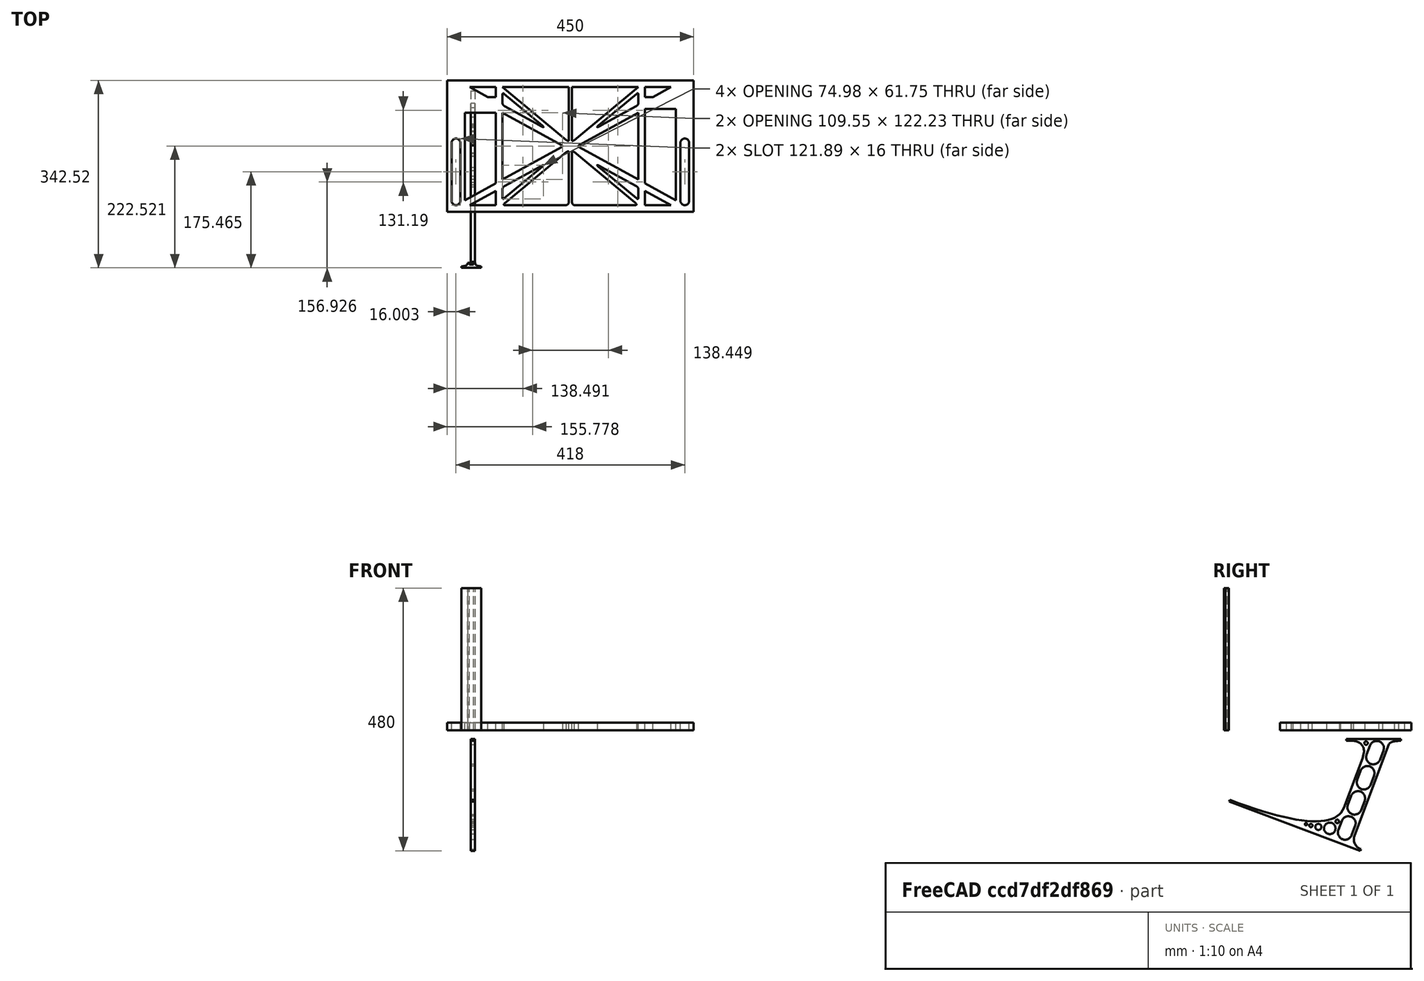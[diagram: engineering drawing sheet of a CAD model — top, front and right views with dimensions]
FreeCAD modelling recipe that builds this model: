
FCSTD DOCUMENT  (FreeCAD 0.19R0.19.2)
Label: laptopStand080
License: All rights reserved
LicenseURL: http://en.wikipedia.org/wiki/All_rights_reserved
objects: Sketcher::SketchObject×3, Part::Extrusion×3
note: 6 computed .brp shape members not serialized (recipe doc carries the construction recipe); baked Part::Feature solids carry a one-line shape summary decoded from their .brp

FEATURE [Sketcher::SketchObject] Sketch
  FullyConstrained = true
  sketch-geometry (196):
    g0: LineSegment StartX=-10.9272 StartY=-82.7794 StartZ=0 EndX=46.0728 EndY=-51.4823 EndZ=0
    g1: LineSegment StartX=366.073 StartY=-91.7794 StartZ=0 EndX=318.073 EndY=-65.424 EndZ=0
    g2: LineSegment StartX=-10.9272 StartY=77.3346 StartZ=0 EndX=-10.9272 EndY=-82.7794 EndZ=0
    g3: LineSegment StartX=375.073 StartY=-82.7794 StartZ=0 EndX=375.073 EndY=83.9235 EndZ=0
    g4: LineSegment StartX=-1.92719 StartY=-91.7794 StartZ=0 EndX=46.0728 EndY=-91.7794 EndZ=0
    g5: LineSegment StartX=318.073 StartY=124.221 StartZ=0 EndX=366.073 EndY=124.221 EndZ=0
    g6: LineSegment StartX=306.073 StartY=124.221 StartZ=0 EndX=189.124 EndY=27.0628 EndZ=0
    g7: LineSegment StartX=175.022 StartY=27.0628 StartZ=0 EndX=58.0728 EndY=124.221 EndZ=0
    g8: LineSegment StartX=306.073 StartY=77.3346 StartZ=0 EndX=306.073 EndY=-44.8935 EndZ=0
    g9: LineSegment StartX=318.073 StartY=83.9235 StartZ=0 EndX=318.073 EndY=-51.4823 EndZ=0
    g10: LineSegment StartX=318.073 StartY=-51.4823 StartZ=0 EndX=375.073 EndY=-82.7794 EndZ=0
    g11: LineSegment StartX=318.073 StartY=-65.424 StartZ=0 EndX=318.073 EndY=-91.7794 EndZ=0
    g12: LineSegment StartX=318.073 StartY=-91.7794 StartZ=0 EndX=366.073 EndY=-91.7794 EndZ=0
    g13: LineSegment StartX=58.0728 StartY=-44.8935 StartZ=0 EndX=58.0728 EndY=77.3346 EndZ=0
    g14: LineSegment StartX=46.0728 StartY=-65.424 StartZ=0 EndX=-1.92719 EndY=-91.7794 EndZ=0
    g15: LineSegment StartX=46.0728 StartY=-65.424 StartZ=0 EndX=46.0728 EndY=-91.7794 EndZ=0
    g16: LineSegment StartX=46.0728 StartY=77.3346 StartZ=0 EndX=46.0728 EndY=-51.4823 EndZ=0
    g17: LineSegment StartX=-42.9272 StartY=136.221 StartZ=0 EndX=-42.9272 EndY=-103.779 EndZ=0
    g18: LineSegment StartX=407.073 StartY=136.221 StartZ=0 EndX=407.073 EndY=-103.779 EndZ=0
    g19: LineSegment StartX=179.022 StartY=27.0628 StartZ=0 EndX=179.022 EndY=124.221 EndZ=0
    g20: LineSegment StartX=185.124 StartY=27.0628 StartZ=0 EndX=185.124 EndY=124.221 EndZ=0
    g21: ArcOfCircle CenterX=-26.9272 CenterY=22.1087 CenterZ=0 NormalX=0 NormalY=0 NormalZ=1 AngleXU=0 Radius=8 StartAngle=1e-16 EndAngle=3.14159
    g22: ArcOfCircle CenterX=-26.9272 CenterY=-83.7794 CenterZ=0 NormalX=0 NormalY=0 NormalZ=1 AngleXU=0 Radius=8 StartAngle=3.14159 EndAngle=6.28319
    g23: LineSegment StartX=-34.9272 StartY=22.1087 StartZ=0 EndX=-34.9272 EndY=-83.7794 EndZ=0
    g24: LineSegment StartX=-18.9272 StartY=22.1087 StartZ=0 EndX=-18.9272 EndY=-83.7794 EndZ=0
    g25: LineSegment StartX=306.073 StartY=124.221 StartZ=0 EndX=185.124 EndY=124.221 EndZ=0
    g26: LineSegment StartX=179.022 StartY=124.221 StartZ=0 EndX=58.0728 EndY=124.221 EndZ=0
    g27: ArcOfCircle CenterX=391.073 CenterY=22.1087 CenterZ=0 NormalX=0 NormalY=0 NormalZ=1 AngleXU=0 Radius=8 StartAngle=-4.4e-15 EndAngle=3.14159
    g28: LineSegment StartX=399.073 StartY=22.1087 StartZ=0 EndX=399.073 EndY=-83.7794 EndZ=0
    g29: LineSegment StartX=383.073 StartY=22.1087 StartZ=0 EndX=383.073 EndY=-83.7794 EndZ=0
    g30: ArcOfCircle CenterX=391.073 CenterY=-83.7794 CenterZ=0 NormalX=0 NormalY=0 NormalZ=1 AngleXU=0 Radius=8 StartAngle=3.14159 EndAngle=6.28319
    g31: Circle CenterX=175.022 CenterY=27.0628 CenterZ=0 NormalX=0 NormalY=0 NormalZ=1 AngleXU=0 Radius=1
    g32: Circle CenterX=179.022 CenterY=24.8665 CenterZ=0 NormalX=0 NormalY=0 NormalZ=1 AngleXU=0 Radius=1
    g33: Circle CenterX=179.022 CenterY=27.0628 CenterZ=0 NormalX=0 NormalY=0 NormalZ=1 AngleXU=0 Radius=1
    g34: BSplineCurve PolesCount=3 KnotsCount=2 Degree=2 IsPeriodic=0
    g35: GeomPoint X=175.022 Y=27.0628 Z=0
    g36: GeomPoint X=179.022 Y=27.0628 Z=0
    g37: Circle CenterX=189.124 CenterY=27.0628 CenterZ=0 NormalX=0 NormalY=0 NormalZ=1 AngleXU=0 Radius=1
    g38: Circle CenterX=185.124 CenterY=24.8665 CenterZ=0 NormalX=0 NormalY=0 NormalZ=1 AngleXU=0 Radius=1
    g39: Circle CenterX=185.124 CenterY=27.0628 CenterZ=0 NormalX=0 NormalY=0 NormalZ=1 AngleXU=0 Radius=1
    g40: BSplineCurve PolesCount=3 KnotsCount=2 Degree=2 IsPeriodic=0
    g41: GeomPoint X=189.124 Y=27.0628 Z=0
    g42: GeomPoint X=185.124 Y=27.0628 Z=0
    g43: Circle CenterX=175.022 CenterY=5.37834 CenterZ=0 NormalX=0 NormalY=0 NormalZ=1 AngleXU=0 Radius=1
    g44: Circle CenterX=179.022 CenterY=7.57463 CenterZ=0 NormalX=0 NormalY=0 NormalZ=1 AngleXU=0 Radius=1
    g45: Circle CenterX=179.022 CenterY=5.34704 CenterZ=0 NormalX=0 NormalY=0 NormalZ=1 AngleXU=0 Radius=1
    g46: BSplineCurve PolesCount=3 KnotsCount=2 Degree=2 IsPeriodic=0
    g47: GeomPoint X=175.022 Y=5.37834 Z=0
    g48: GeomPoint X=179.022 Y=5.34704 Z=0
    g49: Circle CenterX=189.124 CenterY=5.37834 CenterZ=0 NormalX=0 NormalY=0 NormalZ=1 AngleXU=0 Radius=1
    g50: Circle CenterX=185.124 CenterY=7.57463 CenterZ=0 NormalX=0 NormalY=0 NormalZ=1 AngleXU=0 Radius=1
    g51: Circle CenterX=185.124 CenterY=5.34704 CenterZ=0 NormalX=0 NormalY=0 NormalZ=1 AngleXU=0 Radius=1
    g52: BSplineCurve PolesCount=3 KnotsCount=2 Degree=2 IsPeriodic=0
    g53: GeomPoint X=189.124 Y=5.37834 Z=0
    g54: GeomPoint X=185.124 Y=5.34704 Z=0
    g55: Circle CenterX=165.871 CenterY=18.1458 CenterZ=0 NormalX=0 NormalY=0 NormalZ=1 AngleXU=0 Radius=1
    g56: Circle CenterX=169.377 CenterY=16.2206 CenterZ=0 NormalX=0 NormalY=0 NormalZ=1 AngleXU=0 Radius=1
    g57: Circle CenterX=165.871 CenterY=14.2954 CenterZ=0 NormalX=0 NormalY=0 NormalZ=1 AngleXU=0 Radius=1
    g58: BSplineCurve PolesCount=3 KnotsCount=2 Degree=2 IsPeriodic=0
    g59: GeomPoint X=165.871 Y=18.1458 Z=0
    g60: GeomPoint X=165.871 Y=14.2954 Z=0
    g61: Circle CenterX=198.275 CenterY=18.1458 CenterZ=0 NormalX=0 NormalY=0 NormalZ=1 AngleXU=0 Radius=1
    g62: Circle CenterX=194.768 CenterY=16.2206 CenterZ=0 NormalX=0 NormalY=0 NormalZ=1 AngleXU=0 Radius=1
    g63: Circle CenterX=198.275 CenterY=14.2954 CenterZ=0 NormalX=0 NormalY=0 NormalZ=1 AngleXU=0 Radius=1
    g64: BSplineCurve PolesCount=3 KnotsCount=2 Degree=2 IsPeriodic=0
    g65: GeomPoint X=198.275 Y=18.1458 Z=0
    g66: GeomPoint X=198.275 Y=14.2954 Z=0
    g67: LineSegment StartX=165.871 StartY=18.1458 StartZ=0 EndX=58.0728 EndY=77.3346 EndZ=0
    g68: LineSegment StartX=58.0728 StartY=-44.8935 StartZ=0 EndX=165.871 EndY=14.2954 EndZ=0
    g69: LineSegment StartX=198.275 StartY=18.1458 StartZ=0 EndX=306.073 EndY=77.3346 EndZ=0
    g70: LineSegment StartX=198.275 StartY=14.2954 StartZ=0 EndX=306.073 EndY=-44.8935 EndZ=0
    g71: LineSegment StartX=407.073 StartY=-103.779 StartZ=0 EndX=-42.9272 EndY=-103.779 EndZ=0
    g72: LineSegment StartX=407.073 StartY=136.221 StartZ=0 EndX=-42.9272 EndY=136.221 EndZ=0
    g73: LineSegment StartX=46.0728 StartY=77.3346 StartZ=0 EndX=-10.9272 EndY=77.3346 EndZ=0
    g74: LineSegment StartX=46.0728 StartY=105.865 StartZ=0 EndX=31.5028 EndY=105.865 EndZ=0
    g75: LineSegment StartX=46.0728 StartY=124.221 StartZ=0 EndX=46.0728 EndY=105.865 EndZ=0
    g76: LineSegment StartX=-1.92719 StartY=124.221 StartZ=0 EndX=31.5028 EndY=105.865 EndZ=0
    g77: LineSegment StartX=46.0728 StartY=124.221 StartZ=0 EndX=-1.92719 EndY=124.221 EndZ=0
    g78: LineSegment StartX=318.073 StartY=83.9235 StartZ=0 EndX=375.073 EndY=83.9235 EndZ=0
    g79: LineSegment StartX=318.073 StartY=105.865 StartZ=0 EndX=332.643 EndY=105.865 EndZ=0
    g80: LineSegment StartX=332.643 StartY=105.865 StartZ=0 EndX=366.073 EndY=124.221 EndZ=0
    g81: LineSegment StartX=318.073 StartY=124.221 StartZ=0 EndX=318.073 EndY=105.865 EndZ=0
    g82: Circle CenterX=125.607 CenterY=54.1951 CenterZ=0 NormalX=0 NormalY=0 NormalZ=1 AngleXU=0 Radius=1
    g83: Circle CenterX=139.632 CenterY=46.4944 CenterZ=0 NormalX=0 NormalY=0 NormalZ=1 AngleXU=0 Radius=1
    g84: Circle CenterX=127.326 CenterY=56.7187 CenterZ=0 NormalX=0 NormalY=0 NormalZ=1 AngleXU=0 Radius=1
    g85: BSplineCurve PolesCount=3 KnotsCount=2 Degree=2 IsPeriodic=0
    g86: GeomPoint X=125.607 Y=54.1951 Z=0
    g87: GeomPoint X=127.326 Y=56.7187 Z=0
    g88: Circle CenterX=236.821 CenterY=56.7187 CenterZ=0 NormalX=0 NormalY=0 NormalZ=1 AngleXU=0 Radius=1
    g89: Circle CenterX=224.513 CenterY=46.4944 CenterZ=0 NormalX=0 NormalY=0 NormalZ=1 AngleXU=0 Radius=1
    g90: Circle CenterX=238.538 CenterY=54.1951 CenterZ=0 NormalX=0 NormalY=0 NormalZ=1 AngleXU=0 Radius=1
    g91: BSplineCurve PolesCount=3 KnotsCount=2 Degree=2 IsPeriodic=0
    g92: GeomPoint X=236.821 Y=56.7187 Z=0
    g93: GeomPoint X=238.538 Y=54.1951 Z=0
    g94: Circle CenterX=238.538 CenterY=-21.7539 CenterZ=0 NormalX=0 NormalY=0 NormalZ=1 AngleXU=0 Radius=1
    g95: Circle CenterX=224.513 CenterY=-14.0532 CenterZ=0 NormalX=0 NormalY=0 NormalZ=1 AngleXU=0 Radius=1
    g96: Circle CenterX=236.821 CenterY=-24.2775 CenterZ=0 NormalX=0 NormalY=0 NormalZ=1 AngleXU=0 Radius=1
    g97: BSplineCurve PolesCount=3 KnotsCount=2 Degree=2 IsPeriodic=0
    g98: GeomPoint X=238.538 Y=-21.7539 Z=0
    g99: GeomPoint X=236.821 Y=-24.2775 Z=0
    g100: Circle CenterX=125.607 CenterY=-21.7539 CenterZ=0 NormalX=0 NormalY=0 NormalZ=1 AngleXU=0 Radius=1
    g101: Circle CenterX=139.632 CenterY=-14.0532 CenterZ=0 NormalX=0 NormalY=0 NormalZ=1 AngleXU=0 Radius=1
    g102: Circle CenterX=127.325 CenterY=-24.2775 CenterZ=0 NormalX=0 NormalY=0 NormalZ=1 AngleXU=0 Radius=1
    g103: BSplineCurve PolesCount=3 KnotsCount=2 Degree=2 IsPeriodic=0
    g104: GeomPoint X=125.607 Y=-21.7539 Z=0
    g105: GeomPoint X=127.325 Y=-24.2775 Z=0
    g106: Circle CenterX=302.996 CenterY=111.695 CenterZ=0 NormalX=0 NormalY=0 NormalZ=1 AngleXU=0 Radius=1
    g107: Circle CenterX=306.073 CenterY=114.251 CenterZ=0 NormalX=0 NormalY=0 NormalZ=1 AngleXU=0 Radius=1
    g108: Circle CenterX=306.073 CenterY=110.251 CenterZ=0 NormalX=0 NormalY=0 NormalZ=1 AngleXU=0 Radius=1
    g109: BSplineCurve PolesCount=3 KnotsCount=2 Degree=2 IsPeriodic=0
    g110: GeomPoint X=302.996 Y=111.695 Z=0
    g111: GeomPoint X=306.073 Y=110.251 Z=0
    g112: Circle CenterX=306.073 CenterY=95.2763 CenterZ=0 NormalX=0 NormalY=0 NormalZ=1 AngleXU=0 Radius=1
    g113: Circle CenterX=306.073 CenterY=91.2763 CenterZ=0 NormalX=0 NormalY=0 NormalZ=1 AngleXU=0 Radius=1
    g114: Circle CenterX=302.567 CenterY=89.3511 CenterZ=0 NormalX=0 NormalY=0 NormalZ=1 AngleXU=0 Radius=1
    g115: BSplineCurve PolesCount=3 KnotsCount=2 Degree=2 IsPeriodic=0
    g116: GeomPoint X=306.073 Y=95.2763 Z=0
    g117: GeomPoint X=302.567 Y=89.3511 Z=0
    g118: LineSegment StartX=306.073 StartY=110.251 StartZ=0 EndX=306.073 EndY=95.2763 EndZ=0
    g119: LineSegment StartX=302.996 StartY=111.695 StartZ=0 EndX=236.821 EndY=56.7187 EndZ=0
    g120: LineSegment StartX=238.538 StartY=54.1951 StartZ=0 EndX=302.567 EndY=89.3511 EndZ=0
    g121: Circle CenterX=61.1496 CenterY=111.695 CenterZ=0 NormalX=0 NormalY=0 NormalZ=1 AngleXU=0 Radius=1
    g122: Circle CenterX=58.0728 CenterY=114.251 CenterZ=0 NormalX=0 NormalY=0 NormalZ=1 AngleXU=0 Radius=1
    g123: Circle CenterX=58.0728 CenterY=110.251 CenterZ=0 NormalX=0 NormalY=0 NormalZ=1 AngleXU=0 Radius=1
    g124: BSplineCurve PolesCount=3 KnotsCount=2 Degree=2 IsPeriodic=0
    g125: GeomPoint X=61.1496 Y=111.695 Z=0
    g126: GeomPoint X=58.0728 Y=110.251 Z=0
    g127: Circle CenterX=61.5791 CenterY=89.3511 CenterZ=0 NormalX=0 NormalY=0 NormalZ=1 AngleXU=0 Radius=1
    g128: Circle CenterX=58.0728 CenterY=91.2763 CenterZ=0 NormalX=0 NormalY=0 NormalZ=1 AngleXU=0 Radius=1
    g129: Circle CenterX=58.0728 CenterY=95.2763 CenterZ=0 NormalX=0 NormalY=0 NormalZ=1 AngleXU=0 Radius=1
    g130: BSplineCurve PolesCount=3 KnotsCount=2 Degree=2 IsPeriodic=0
    g131: GeomPoint X=61.5791 Y=89.3511 Z=0
    g132: GeomPoint X=58.0728 Y=95.2763 Z=0
    g133: LineSegment StartX=58.0728 StartY=110.251 StartZ=0 EndX=58.0728 EndY=95.2763 EndZ=0
    g134: LineSegment StartX=61.1496 StartY=111.695 StartZ=0 EndX=127.326 EndY=56.7187 EndZ=0
    g135: LineSegment StartX=125.607 StartY=54.1951 StartZ=0 EndX=61.5791 EndY=89.3511 EndZ=0
    g136: Circle CenterX=61.5791 CenterY=-56.9099 CenterZ=0 NormalX=0 NormalY=0 NormalZ=1 AngleXU=0 Radius=1
    g137: Circle CenterX=58.0728 CenterY=-58.8351 CenterZ=0 NormalX=0 NormalY=0 NormalZ=1 AngleXU=0 Radius=1
    g138: Circle CenterX=58.0728 CenterY=-62.8351 CenterZ=0 NormalX=0 NormalY=0 NormalZ=1 AngleXU=0 Radius=1
    g139: BSplineCurve PolesCount=3 KnotsCount=2 Degree=2 IsPeriodic=0
    g140: GeomPoint X=61.5791 Y=-56.9099 Z=0
    g141: GeomPoint X=58.0728 Y=-62.8351 Z=0
    g142: Circle CenterX=58.0728 CenterY=-77.8102 CenterZ=0 NormalX=0 NormalY=0 NormalZ=1 AngleXU=0 Radius=1
    g143: Circle CenterX=58.0728 CenterY=-81.8102 CenterZ=0 NormalX=0 NormalY=0 NormalZ=1 AngleXU=0 Radius=1
    g144: Circle CenterX=61.1496 CenterY=-79.2541 CenterZ=0 NormalX=0 NormalY=0 NormalZ=1 AngleXU=0 Radius=1
    g145: BSplineCurve PolesCount=3 KnotsCount=2 Degree=2 IsPeriodic=0
    g146: GeomPoint X=58.0728 Y=-77.8102 Z=0
    g147: GeomPoint X=61.1496 Y=-79.2541 Z=0
    g148: LineSegment StartX=58.0728 StartY=-62.8351 StartZ=0 EndX=58.0728 EndY=-77.8102 EndZ=0
    g149: LineSegment StartX=61.1496 StartY=-79.2541 StartZ=0 EndX=127.325 EndY=-24.2775 EndZ=0
    g150: LineSegment StartX=125.607 StartY=-21.7539 StartZ=0 EndX=61.5791 EndY=-56.9099 EndZ=0
    g151: Circle CenterX=302.567 CenterY=-56.9099 CenterZ=0 NormalX=0 NormalY=0 NormalZ=1 AngleXU=0 Radius=1
    g152: Circle CenterX=306.073 CenterY=-58.8351 CenterZ=0 NormalX=0 NormalY=0 NormalZ=1 AngleXU=0 Radius=1
    g153: Circle CenterX=306.073 CenterY=-62.8351 CenterZ=0 NormalX=0 NormalY=0 NormalZ=1 AngleXU=0 Radius=1
    g154: BSplineCurve PolesCount=3 KnotsCount=2 Degree=2 IsPeriodic=0
    g155: GeomPoint X=302.567 Y=-56.9099 Z=0
    g156: GeomPoint X=306.073 Y=-62.8351 Z=0
    g157: Circle CenterX=302.996 CenterY=-79.2541 CenterZ=0 NormalX=0 NormalY=0 NormalZ=1 AngleXU=0 Radius=1
    g158: Circle CenterX=306.073 CenterY=-81.8102 CenterZ=0 NormalX=0 NormalY=0 NormalZ=1 AngleXU=0 Radius=1
    g159: Circle CenterX=306.073 CenterY=-77.8102 CenterZ=0 NormalX=0 NormalY=0 NormalZ=1 AngleXU=0 Radius=1
    g160: BSplineCurve PolesCount=3 KnotsCount=2 Degree=2 IsPeriodic=0
    g161: GeomPoint X=302.996 Y=-79.2541 Z=0
    g162: GeomPoint X=306.073 Y=-77.8102 Z=0
    g163: LineSegment StartX=306.073 StartY=-62.8351 StartZ=0 EndX=306.073 EndY=-77.8102 EndZ=0
    g164: LineSegment StartX=302.996 StartY=-79.2541 StartZ=0 EndX=236.821 EndY=-24.2775 EndZ=0
    g165: LineSegment StartX=238.538 StartY=-21.7539 StartZ=0 EndX=302.567 EndY=-56.9099 EndZ=0
    g166: Circle CenterX=61.6457 CenterY=-88.8112 CenterZ=0 NormalX=0 NormalY=0 NormalZ=1 AngleXU=0 Radius=1
    g167: Circle CenterX=58.0728 CenterY=-91.7794 CenterZ=0 NormalX=0 NormalY=0 NormalZ=1 AngleXU=0 Radius=1
    g168: Circle CenterX=63.9135 CenterY=-91.7794 CenterZ=0 NormalX=0 NormalY=0 NormalZ=1 AngleXU=0 Radius=1
    g169: BSplineCurve PolesCount=3 KnotsCount=2 Degree=2 IsPeriodic=0
    g170: GeomPoint X=61.6457 Y=-88.8112 Z=0
    g171: GeomPoint X=63.9135 Y=-91.7794 Z=0
    g172: Circle CenterX=179.022 CenterY=-85.8163 CenterZ=0 NormalX=0 NormalY=0 NormalZ=1 AngleXU=0 Radius=1
    g173: Circle CenterX=179.022 CenterY=-91.7794 CenterZ=0 NormalX=0 NormalY=0 NormalZ=1 AngleXU=0 Radius=1
    g174: Circle CenterX=171.895 CenterY=-91.7794 CenterZ=0 NormalX=0 NormalY=0 NormalZ=1 AngleXU=0 Radius=1
    g175: BSplineCurve PolesCount=3 KnotsCount=2 Degree=2 IsPeriodic=0
    g176: GeomPoint X=179.022 Y=-85.8163 Z=0
    g177: GeomPoint X=171.895 Y=-91.7794 Z=0
    g178: Circle CenterX=185.124 CenterY=-86.2028 CenterZ=0 NormalX=0 NormalY=0 NormalZ=1 AngleXU=0 Radius=1
    g179: Circle CenterX=185.124 CenterY=-91.7794 CenterZ=0 NormalX=0 NormalY=0 NormalZ=1 AngleXU=0 Radius=1
    g180: Circle CenterX=191.747 CenterY=-91.7794 CenterZ=0 NormalX=0 NormalY=0 NormalZ=1 AngleXU=0 Radius=1
    g181: BSplineCurve PolesCount=3 KnotsCount=2 Degree=2 IsPeriodic=0
    g182: GeomPoint X=185.124 Y=-86.2028 Z=0
    g183: GeomPoint X=191.747 Y=-91.7794 Z=0
    g184: Circle CenterX=299.888 CenterY=-86.6413 CenterZ=0 NormalX=0 NormalY=0 NormalZ=1 AngleXU=0 Radius=1
    g185: Circle CenterX=306.073 CenterY=-91.7794 CenterZ=0 NormalX=0 NormalY=0 NormalZ=1 AngleXU=0 Radius=1
    g186: Circle CenterX=298.776 CenterY=-91.7794 CenterZ=0 NormalX=0 NormalY=0 NormalZ=1 AngleXU=0 Radius=1
    g187: BSplineCurve PolesCount=3 KnotsCount=2 Degree=2 IsPeriodic=0
    g188: GeomPoint X=299.888 Y=-86.6413 Z=0
    g189: GeomPoint X=298.776 Y=-91.7794 Z=0
    g190: LineSegment StartX=189.124 StartY=5.37834 StartZ=0 EndX=299.888 EndY=-86.6413 EndZ=0
    g191: LineSegment StartX=298.776 StartY=-91.7794 StartZ=0 EndX=191.747 EndY=-91.7794 EndZ=0
    g192: LineSegment StartX=185.124 StartY=-86.2028 StartZ=0 EndX=185.124 EndY=5.34704 EndZ=0
    g193: LineSegment StartX=179.022 StartY=5.34704 StartZ=0 EndX=179.022 EndY=-85.8163 EndZ=0
    g194: LineSegment StartX=171.895 StartY=-91.7794 StartZ=0 EndX=63.9135 EndY=-91.7794 EndZ=0
    g195: LineSegment StartX=61.6457 StartY=-88.8112 StartZ=0 EndX=175.022 EndY=5.37834 EndZ=0
  constraints (339):
    c: Horizontal(g4)
    c: Horizontal(g5)
    c: Coincident(g9,g10)
    c: Coincident(g11,g1)
    c: Tangent(g9,g11)
    c: Coincident(g15,g14)
    c: Coincident(g0,g16)
    c: Block(g7)
    c: Block(g6)
    c: Block(g10)
    c: Block(g3)
    c: Block(g1)
    c: Block(g11)
    c: Block(g15)
    c: Block(g14)
    c: Block(g0)
    c: Block(g2)
    c: Block(g8)
    c: Block(g5)
    c: Block(g12)
    c: Block(g4)
    c: Vertical(g17)
    c: Vertical(g18)
    c: Block(g18)
    c: Block(g17)
    c: Vertical(g19)
    c: Vertical(g20)
    c: Block(g19)
    c: Block(g20)
    c: Tangent(g21,g24) = 1.5708
    c: Tangent(g21,g23) = -1.5708
    c: Tangent(g23,g22) = -1.5708
    c: Tangent(g24,g22) = 1.5708
    c: Vertical(g23)
    c: Equal(g21,g22)
    c: Block(g24)
    c: Block(g23)
    c: Coincident(g25,g6)
    c: Coincident(g25,g20)
    c: Horizontal(g25)
    c: Coincident(g26,g19)
    c: Coincident(g26,g7)
    c: Horizontal(g26)
    c: Tangent(g27,g28) = 1.5708
    c: Tangent(g28,g30) = 1.5708
    c: Equal(g27,g30)
    c: Coincident(g29,g27)
    c: Coincident(g29,g30)
    c: Block(g28)
    c: Block(g29)
    c: Coincident(g34,g7)
    c: Weight(g31) = 1
    c: Equal(g31,g32)
    c: Equal(g31,g33)
    c: Coincident(g34,g19)
    c: InternalAlignment(g31,g34)
    c: InternalAlignment(g32,g34)
    c: InternalAlignment(g33,g34)
    c: InternalAlignment(g35,g34)
    c: InternalAlignment(g36,g34)
    c: Coincident(g40,g6)
    c: Weight(g37) = 1
    c: Equal(g37,g38)
    c: Equal(g37,g39)
    c: Coincident(g40,g20)
    c: InternalAlignment(g37,g40)
    c: InternalAlignment(g38,g40)
    c: InternalAlignment(g39,g40)
    c: InternalAlignment(g41,g40)
    c: InternalAlignment(g42,g40)
    c: Block(g40)
    c: Block(g34)
    c: Weight(g43) = 1
    c: Equal(g43,g44)
    c: Equal(g43,g45)
    c: InternalAlignment(g43,g46)
    c: InternalAlignment(g44,g46)
    c: InternalAlignment(g45,g46)
    c: InternalAlignment(g47,g46)
    c: InternalAlignment(g48,g46)
    c: Weight(g49) = 1
    c: Equal(g49,g50)
    c: Equal(g49,g51)
    c: InternalAlignment(g49,g52)
    c: InternalAlignment(g50,g52)
    c: InternalAlignment(g51,g52)
    c: InternalAlignment(g53,g52)
    c: InternalAlignment(g54,g52)
    c: Block(g52)
    c: Block(g46)
    c: Weight(g55) = 1
    c: Equal(g55,g56)
    c: Equal(g55,g57)
    c: InternalAlignment(g55,g58)
    c: InternalAlignment(g56,g58)
    c: InternalAlignment(g57,g58)
    c: InternalAlignment(g59,g58)
    c: InternalAlignment(g60,g58)
    c: Weight(g61) = 1
    c: Equal(g61,g62)
    c: Equal(g61,g63)
    c: InternalAlignment(g61,g64)
    c: InternalAlignment(g62,g64)
    c: InternalAlignment(g63,g64)
    c: InternalAlignment(g65,g64)
    c: InternalAlignment(g66,g64)
    c: Block(g58)
    c: Block(g64)
    c: Coincident(g67,g58)
    c: Coincident(g67,g13)
    c: Coincident(g68,g13)
    c: Coincident(g68,g58)
    c: Coincident(g69,g64)
    c: Coincident(g69,g8)
    c: Coincident(g70,g64)
    c: Coincident(g70,g8)
    c: Block(g13)
    c: Coincident(g71,g18)
    c: Coincident(g71,g17)
    c: Horizontal(g71)
    c: Distance(g71) = 450
    c: Coincident(g72,g18)
    c: Coincident(g72,g17)
    c: Horizontal(g72)
    c: Horizontal(g73)
    c: Coincident(g16,g73)
    c: Horizontal(g74)
    c: Vertical(g75)
    c: Block(g75)
    c: Block(g74)
    c: Block(g73)
    c: Distance(g75) = 18.3554
    c: Coincident(g77,g75)
    c: Coincident(g77,g76)
    c: Horizontal(g77)
    c: Block(g77)
    c: Block(g76)
    c: Coincident(g74,g76)
    c: Coincident(g2,g73)
    c: Coincident(g78,g9)
    c: Horizontal(g78)
    c: Horizontal(g79)
    c: Block(g78)
    c: Coincident(g80,g5)
    c: Coincident(g81,g5)
    c: Coincident(g81,g79)
    c: Vertical(g81)
    c: Block(g81)
    c: Coincident(g79,g80)
    c: Block(g80)
    c: Coincident(g3,g78)
    c: Weight(g82) = 1
    c: Equal(g82,g83)
    c: Equal(g82,g84)
    c: InternalAlignment(g82,g85)
    c: InternalAlignment(g83,g85)
    c: InternalAlignment(g84,g85)
    c: InternalAlignment(g86,g85)
    c: InternalAlignment(g87,g85)
    c: Block(g85)
    c: Weight(g88) = 1
    c: Equal(g88,g89)
    c: Equal(g88,g90)
    c: InternalAlignment(g88,g91)
    c: InternalAlignment(g89,g91)
    c: InternalAlignment(g90,g91)
    c: InternalAlignment(g92,g91)
    c: InternalAlignment(g93,g91)
    c: Block(g91)
    c: Weight(g94) = 1
    c: Equal(g94,g95)
    c: Equal(g94,g96)
    c: InternalAlignment(g94,g97)
    c: InternalAlignment(g95,g97)
    c: InternalAlignment(g96,g97)
    c: InternalAlignment(g98,g97)
    c: InternalAlignment(g99,g97)
    c: Block(g97)
    c: Weight(g100) = 1
    c: Equal(g100,g101)
    c: Equal(g100,g102)
    c: InternalAlignment(g100,g103)
    c: InternalAlignment(g101,g103)
    c: InternalAlignment(g102,g103)
    c: InternalAlignment(g104,g103)
    c: InternalAlignment(g105,g103)
    c: Block(g103)
    c: Weight(g106) = 1
    c: Equal(g106,g107)
    c: Equal(g106,g108)
    c: InternalAlignment(g106,g109)
    c: InternalAlignment(g107,g109)
    c: InternalAlignment(g108,g109)
    c: InternalAlignment(g110,g109)
    c: InternalAlignment(g111,g109)
    c: Weight(g112) = 1
    c: Equal(g112,g113)
    c: Equal(g112,g114)
    c: InternalAlignment(g112,g115)
    c: InternalAlignment(g113,g115)
    c: InternalAlignment(g114,g115)
    c: InternalAlignment(g116,g115)
    c: InternalAlignment(g117,g115)
    c: Block(g109)
    c: Block(g115)
    c: Coincident(g118,g109)
    c: Coincident(g118,g115)
    c: Vertical(g118)
    c: Coincident(g119,g109)
    c: Coincident(g119,g91)
    c: Coincident(g120,g91)
    c: Coincident(g120,g115)
    c: Weight(g121) = 1
    c: Equal(g121,g122)
    c: Equal(g121,g123)
    c: InternalAlignment(g121,g124)
    c: InternalAlignment(g122,g124)
    c: InternalAlignment(g123,g124)
    c: InternalAlignment(g125,g124)
    c: InternalAlignment(g126,g124)
    c: Weight(g127) = 1
    c: Equal(g127,g128)
    c: Equal(g127,g129)
    c: InternalAlignment(g127,g130)
    c: InternalAlignment(g128,g130)
    c: InternalAlignment(g129,g130)
    c: InternalAlignment(g131,g130)
    c: InternalAlignment(g132,g130)
    c: Block(g124)
    c: Block(g130)
    c: Coincident(g133,g124)
    c: Coincident(g133,g130)
    c: Vertical(g133)
    c: Coincident(g134,g124)
    c: Coincident(g134,g85)
    c: Coincident(g135,g85)
    c: Coincident(g135,g130)
    c: Weight(g136) = 1
    c: Equal(g136,g137)
    c: Equal(g136,g138)
    c: InternalAlignment(g136,g139)
    c: InternalAlignment(g137,g139)
    c: InternalAlignment(g138,g139)
    c: InternalAlignment(g140,g139)
    c: InternalAlignment(g141,g139)
    c: Weight(g142) = 1
    c: Equal(g142,g143)
    c: Equal(g142,g144)
    c: InternalAlignment(g142,g145)
    c: InternalAlignment(g143,g145)
    c: InternalAlignment(g144,g145)
    c: InternalAlignment(g146,g145)
    c: InternalAlignment(g147,g145)
    c: Block(g139)
    c: Block(g145)
    c: Coincident(g148,g139)
    c: Coincident(g148,g145)
    c: Vertical(g148)
    c: Coincident(g149,g145)
    c: Coincident(g149,g103)
    c: Coincident(g150,g103)
    c: Coincident(g150,g139)
    c: Weight(g151) = 1
    c: Equal(g151,g152)
    c: Equal(g151,g153)
    c: InternalAlignment(g151,g154)
    c: InternalAlignment(g152,g154)
    c: InternalAlignment(g153,g154)
    c: InternalAlignment(g155,g154)
    c: InternalAlignment(g156,g154)
    c: Weight(g157) = 1
    c: Equal(g157,g158)
    c: Equal(g157,g159)
    c: InternalAlignment(g157,g160)
    c: InternalAlignment(g158,g160)
    c: InternalAlignment(g159,g160)
    c: InternalAlignment(g161,g160)
    c: InternalAlignment(g162,g160)
    c: Block(g154)
    c: Block(g160)
    c: Coincident(g163,g154)
    c: Coincident(g163,g160)
    c: Vertical(g163)
    c: Coincident(g164,g160)
    c: Coincident(g164,g97)
    c: Coincident(g165,g97)
    c: Coincident(g165,g154)
    c: Weight(g166) = 1
    c: Equal(g166,g167)
    c: Equal(g166,g168)
    c: InternalAlignment(g166,g169)
    c: InternalAlignment(g167,g169)
    c: InternalAlignment(g168,g169)
    c: InternalAlignment(g170,g169)
    c: InternalAlignment(g171,g169)
    c: Weight(g172) = 1
    c: Equal(g172,g173)
    c: Equal(g172,g174)
    c: InternalAlignment(g172,g175)
    c: InternalAlignment(g173,g175)
    c: InternalAlignment(g174,g175)
    c: InternalAlignment(g176,g175)
    c: InternalAlignment(g177,g175)
    c: Weight(g178) = 1
    c: Equal(g178,g179)
    c: Equal(g178,g180)
    c: InternalAlignment(g178,g181)
    c: InternalAlignment(g179,g181)
    c: InternalAlignment(g180,g181)
    c: InternalAlignment(g182,g181)
    c: InternalAlignment(g183,g181)
    c: Weight(g184) = 1
    c: Equal(g184,g185)
    c: Equal(g184,g186)
    c: InternalAlignment(g184,g187)
    c: InternalAlignment(g185,g187)
    c: InternalAlignment(g186,g187)
    c: InternalAlignment(g188,g187)
    c: InternalAlignment(g189,g187)
    c: Block(g187)
    c: Block(g181)
    c: Block(g175)
    c: Block(g169)
    c: Coincident(g190,g52)
    c: Coincident(g190,g187)
    c: Coincident(g191,g187)
    c: Coincident(g191,g181)
    c: Horizontal(g191)
    c: Coincident(g192,g181)
    c: Coincident(g192,g52)
    c: Vertical(g192)
    c: Coincident(g193,g46)
    c: Coincident(g193,g175)
    c: Vertical(g193)
    c: Coincident(g194,g175)
    c: Coincident(g194,g169)
    c: Horizontal(g194)
    c: Coincident(g195,g169)
    c: Coincident(g195,g46)
FEATURE [Sketcher::SketchObject] Sketch001
  FullyConstrained = true
  MapMode = 4
  Placement = pos=(0,0,0) rot=(0.57735,0.57735,0.57735;2.0944rad)
  Support = -> [Sketch]
  sketch-geometry (46):
    g0: BSplineCurve PolesCount=3 KnotsCount=2 Degree=2 IsPeriodic=0
    g1: ArcOfCircle CenterX=73.1223 CenterY=-32.291 CenterZ=0 NormalX=0 NormalY=0 NormalZ=1 AngleXU=0 Radius=13 StartAngle=5.92268 EndAngle=9.06428
    g2: ArcOfCircle CenterX=66.7816 CenterY=-49.1439 CenterZ=0 NormalX=0 NormalY=0 NormalZ=1 AngleXU=0 Radius=13 StartAngle=2.78068 EndAngle=5.92131
    g3: ArcOfCircle CenterX=55.9263 CenterY=-78.1807 CenterZ=0 NormalX=0 NormalY=0 NormalZ=1 AngleXU=0 Radius=13 StartAngle=5.92268 EndAngle=9.06428
    g4: ArcOfCircle CenterX=49.5884 CenterY=-95.0342 CenterZ=0 NormalX=0 NormalY=0 NormalZ=1 AngleXU=0 Radius=13 StartAngle=2.78068 EndAngle=5.92131
    g5: ArcOfCircle CenterX=38.7206 CenterY=-124.067 CenterZ=0 NormalX=0 NormalY=0 NormalZ=1 AngleXU=0 Radius=13 StartAngle=5.92268 EndAngle=9.06428
    g6: ArcOfCircle CenterX=32.3875 CenterY=-140.92 CenterZ=0 NormalX=0 NormalY=0 NormalZ=1 AngleXU=0 Radius=13 StartAngle=2.78068 EndAngle=5.92131
    g7: ArcOfCircle CenterX=21.4715 CenterY=-169.934 CenterZ=0 NormalX=0 NormalY=0 NormalZ=1 AngleXU=0 Radius=13 StartAngle=5.92268 EndAngle=9.06428
    g8: ArcOfCircle CenterX=15.1336 CenterY=-186.787 CenterZ=0 NormalX=0 NormalY=0 NormalZ=1 AngleXU=0 Radius=13 StartAngle=2.78068 EndAngle=5.92131
    g9-g12: Circle x4 (B-spline internal-alignment scaffolding for g13; pole/knot coordinates omitted)
    g13: BSplineCurve PolesCount=4 KnotsCount=2 Degree=3 IsPeriodic=0
    g14: GeomPoint X=28.8094 Y=-19.0875 Z=0
    g15: GeomPoint X=47.0443 Y=-50.4712 Z=0
    g16: Circle CenterX=53.5586 CenterY=-23.2695 CenterZ=0 NormalX=0 NormalY=0 NormalZ=1 AngleXU=0 Radius=3.24518
    g17: Circle CenterX=-195.441 CenterY=-127.082 CenterZ=0 NormalX=0 NormalY=0 NormalZ=1 AngleXU=0 Radius=1
    g18: Circle CenterX=-8.24091 CenterY=-197.481 CenterZ=0 NormalX=0 NormalY=0 NormalZ=1 AngleXU=0 Radius=1
    g19: Circle CenterX=12.8789 CenterY=-141.321 CenterZ=0 NormalX=0 NormalY=0 NormalZ=1 AngleXU=0 Radius=1
    g20: BSplineCurve PolesCount=3 KnotsCount=2 Degree=2 IsPeriodic=0
    g21: GeomPoint X=-195.441 Y=-127.082 Z=0
    g22: GeomPoint X=12.8789 Y=-141.321 Z=0
    g23: Circle CenterX=-12.8016 CenterY=-179.036 CenterZ=0 NormalX=0 NormalY=0 NormalZ=1 AngleXU=0 Radius=10.5072
    g24: Circle CenterX=0.933922 CenterY=-166.43 CenterZ=0 NormalX=0 NormalY=0 NormalZ=1 AngleXU=0 Radius=3.26661
    g25: Circle CenterX=-33.5518 CenterY=-176.44 CenterZ=0 NormalX=0 NormalY=0 NormalZ=1 AngleXU=0 Radius=5.64388
    g26: Circle CenterX=-47.2366 CenterY=-173.859 CenterZ=0 NormalX=0 NormalY=0 NormalZ=1 AngleXU=0 Radius=3.01653
    g27: Circle CenterX=-56.2595 CenterY=-171.456 CenterZ=0 NormalX=0 NormalY=0 NormalZ=1 AngleXU=0 Radius=2.12826
    g28: ArcOfCircle CenterX=51.2151 CenterY=-198.473 CenterZ=0 NormalX=0 NormalY=0 NormalZ=1 AngleXU=0 Radius=20 StartAngle=2.78189 EndAngle=4.35269
    g29: LineSegment StartX=32.4951 StartY=-191.433 StartZ=0 EndX=94.6578 EndY=-26.1352 EndZ=0
    g30: LineSegment StartX=43.1192 StartY=-220.001 StartZ=0 EndX=-196.497 EndY=-129.89 EndZ=0
    g31: LineSegment StartX=43.1192 StartY=-220.001 StartZ=0 EndX=44.1752 EndY=-217.193 EndZ=0
    g32: LineSegment StartX=117.223 StartY=-19.0875 StartZ=0 EndX=117.223 EndY=-16.0875 EndZ=0
    g33: LineSegment StartX=117.223 StartY=-16.0875 StartZ=0 EndX=17.2232 EndY=-16.0875 EndZ=0
    g34: LineSegment StartX=17.2232 StartY=-16.0875 StartZ=0 EndX=17.2232 EndY=-19.0875 EndZ=0
    g35: LineSegment StartX=28.8094 StartY=-19.0875 StartZ=0 EndX=17.2232 EndY=-19.0875 EndZ=0
    g36: LineSegment StartX=47.0443 StartY=-50.4712 StartZ=0 EndX=12.8789 EndY=-141.321 EndZ=0
    g37: LineSegment StartX=-195.441 StartY=-127.082 StartZ=0 EndX=-196.497 EndY=-129.89 EndZ=0
    g38: LineSegment StartX=85.2866 StartY=-36.8766 StartZ=0 EndX=78.9396 EndY=-53.7463 EndZ=0
    g39: LineSegment StartX=60.9579 StartY=-27.7053 StartZ=0 EndX=54.6191 EndY=-44.5532 EndZ=0
    g40: LineSegment StartX=68.0907 StartY=-82.7664 StartZ=0 EndX=61.7465 EndY=-99.6365 EndZ=0
    g41: LineSegment StartX=43.7619 StartY=-73.595 StartZ=0 EndX=37.426 EndY=-90.4435 EndZ=0
    g42: LineSegment StartX=50.885 StartY=-128.652 StartZ=0 EndX=44.5456 EndY=-145.522 EndZ=0
    g43: LineSegment StartX=26.5562 StartY=-119.481 StartZ=0 EndX=20.2251 EndY=-136.329 EndZ=0
    g44: LineSegment StartX=9.3071 StartY=-165.349 StartZ=0 EndX=2.97115 EndY=-182.197 EndZ=0
    g45: LineSegment StartX=33.6358 StartY=-174.52 StartZ=0 EndX=27.2917 EndY=-191.39 EndZ=0
  constraints (71):
    c: Block(g0)
    c: Block(g1)
    c: Block(g2)
    c: Block(g4)
    c: Block(g3)
    c: Block(g6)
    c: Block(g5)
    c: Block(g8)
    c: Block(g7)
    c: Weight(g9) = 1
    c: Equal(g9,g10)
    c: Equal(g9,g11)
    c: Equal(g9,g12)
    c: InternalAlignment(g9-g12 -> g13) x4
    c: InternalAlignment(g14,g13)
    c: InternalAlignment(g15,g13)
    c: Block(g16)
    c: Weight(g17) = 1
    c: Equal(g17,g18)
    c: Equal(g17,g19)
    c: InternalAlignment(g17,g20)
    c: InternalAlignment(g18,g20)
    c: InternalAlignment(g19,g20)
    c: InternalAlignment(g21,g20)
    c: InternalAlignment(g22,g20)
    c: Block(g20)
    c: Block(g23)
    c: Block(g24)
    c: Block(g25)
    c: Block(g26)
    c: Block(g27)
    c: Block(g28)
    c: Coincident(g29,g28)
    c: Coincident(g29,g0)
    c: Block(g13)
    c: Coincident(g31,g30)
    c: Coincident(g31,g28)
    c: Block(g31)
    c: Coincident(g32,g0)
    c: Vertical(g32)
    c: Coincident(g33,g32)
    c: Horizontal(g33)
    c: Coincident(g34,g33)
    c: Vertical(g34)
    c: Block(g33)
    c: Coincident(g35,g13)
    c: Coincident(g35,g34)
    c: Horizontal(g35)
    c: Coincident(g36,g13)
    c: Coincident(g36,g20)
    c: Coincident(g37,g20)
    c: Coincident(g37,g30)
    c: Block(g30)
    c: Coincident(g38,g1)
    c: Coincident(g38,g2)
    c: Coincident(g39,g1)
    c: Coincident(g39,g2)
    c: Coincident(g40,g3)
    c: Coincident(g40,g4)
    c: Coincident(g41,g3)
    c: Coincident(g41,g4)
    c: Coincident(g42,g5)
    c: Coincident(g42,g6)
    c: Coincident(g43,g5)
    c: Coincident(g43,g6)
    c: Coincident(g44,g7)
    c: Coincident(g44,g8)
    c: Coincident(g45,g7)
    c: Coincident(g45,g8)
    c: Distance(g30) = 256
    c: Distance(g33) = 100
FEATURE [Part::Extrusion] Extrude002
  Base = -> Sketch001
  Dir = (1,0,0)
  DirMode = 2
  FaceMakerClass = Part::FaceMakerBullseye
  LengthFwd = 8
  LengthRev = 0
  Solid = true
  Symmetric = false
FEATURE [Sketcher::SketchObject] Sketch002
  FullyConstrained = true
  sketch-geometry (20):
    g0: LineSegment StartX=-2.77179 StartY=-200.304 StartZ=0 EndX=5.22821 EndY=-200.304 EndZ=0
    g1: LineSegment StartX=5.22821 StartY=-200.304 StartZ=0 EndX=5.22821 EndY=-197.304 EndZ=0
    g2: LineSegment StartX=-2.77179 StartY=-200.304 StartZ=0 EndX=-2.77179 EndY=-197.304 EndZ=0
    g3: LineSegment StartX=5.22821 StartY=-197.304 StartZ=0 EndX=8.22821 EndY=-197.304 EndZ=0
    g4: LineSegment StartX=-2.77179 StartY=-197.304 StartZ=0 EndX=-5.77179 EndY=-197.304 EndZ=0
    g5: LineSegment StartX=19.2282 StartY=-203.304 StartZ=0 EndX=19.2282 EndY=-206.304 EndZ=0
    g6: LineSegment StartX=-16.7718 StartY=-203.304 StartZ=0 EndX=-16.7718 EndY=-206.304 EndZ=0
    g7: LineSegment StartX=-16.7718 StartY=-206.304 StartZ=0 EndX=19.2282 EndY=-206.304 EndZ=0
    g8: Circle CenterX=-16.7718 CenterY=-203.304 CenterZ=0 NormalX=0 NormalY=0 NormalZ=1 AngleXU=0 Radius=1
    g9: Circle CenterX=-5.77179 CenterY=-203.304 CenterZ=0 NormalX=0 NormalY=0 NormalZ=1 AngleXU=0 Radius=1
    g10: Circle CenterX=-5.77179 CenterY=-197.304 CenterZ=0 NormalX=0 NormalY=0 NormalZ=1 AngleXU=0 Radius=1
    g11: BSplineCurve PolesCount=3 KnotsCount=2 Degree=2 IsPeriodic=0
    g12: GeomPoint X=-16.7718 Y=-203.304 Z=0
    g13: GeomPoint X=-5.77179 Y=-197.304 Z=0
    g14: Circle CenterX=19.2282 CenterY=-203.304 CenterZ=0 NormalX=0 NormalY=0 NormalZ=1 AngleXU=0 Radius=1
    g15: Circle CenterX=8.22821 CenterY=-203.304 CenterZ=0 NormalX=0 NormalY=0 NormalZ=1 AngleXU=0 Radius=1
    g16: Circle CenterX=8.22821 CenterY=-197.304 CenterZ=0 NormalX=0 NormalY=0 NormalZ=1 AngleXU=0 Radius=1
    g17: BSplineCurve PolesCount=3 KnotsCount=2 Degree=2 IsPeriodic=0
    g18: GeomPoint X=19.2282 Y=-203.304 Z=0
    g19: GeomPoint X=8.22821 Y=-197.304 Z=0
  constraints (41):
    c: Horizontal(g0)
    c: Distance(g0) = 8
    c: Coincident(g1,g0)
    c: Vertical(g1)
    c: Distance(g1) = 3
    c: Coincident(g2,g0)
    c: Vertical(g2)
    c: Distance(g2) = 3
    c: Coincident(g3,g1)
    c: Horizontal(g3)
    c: Distance(g3) = 3
    c: Coincident(g4,g2)
    c: Horizontal(g4)
    c: Distance(g4) = 3
    c: Vertical(g5)
    c: Vertical(g6)
    c: Coincident(g7,g6)
    c: Coincident(g7,g5)
    c: Weight(g8) = 1
    c: Equal(g8,g9)
    c: Equal(g8,g10)
    c: Coincident(g11,g4)
    c: InternalAlignment(g8,g11)
    c: InternalAlignment(g9,g11)
    c: InternalAlignment(g10,g11)
    c: InternalAlignment(g12,g11)
    c: InternalAlignment(g13,g11)
    c: Coincident(g17,g5)
    c: Weight(g14) = 1
    c: Equal(g14,g15)
    c: Equal(g14,g16)
    c: Coincident(g17,g3)
    c: InternalAlignment(g14,g17)
    c: InternalAlignment(g15,g17)
    c: InternalAlignment(g16,g17)
    c: InternalAlignment(g18,g17)
    c: InternalAlignment(g19,g17)
    c: Block(g7)
    c: Block(g17)
    c: Block(g11)
    c: Block(g6)
FEATURE [Part::Extrusion] Extrude003
  Base = -> Sketch002
  Dir = (0,0,1)
  DirMode = 2
  FaceMakerClass = Part::FaceMakerBullseye
  LengthFwd = 260
  LengthRev = 0
  Solid = true
  Symmetric = false
FEATURE [Part::Extrusion] Extrude
  Base = -> Sketch
  Dir = (0,0,1)
  DirMode = 2
  FaceMakerClass = Part::FaceMakerBullseye
  LengthFwd = 14
  LengthRev = 0
  Solid = true
  Symmetric = false
